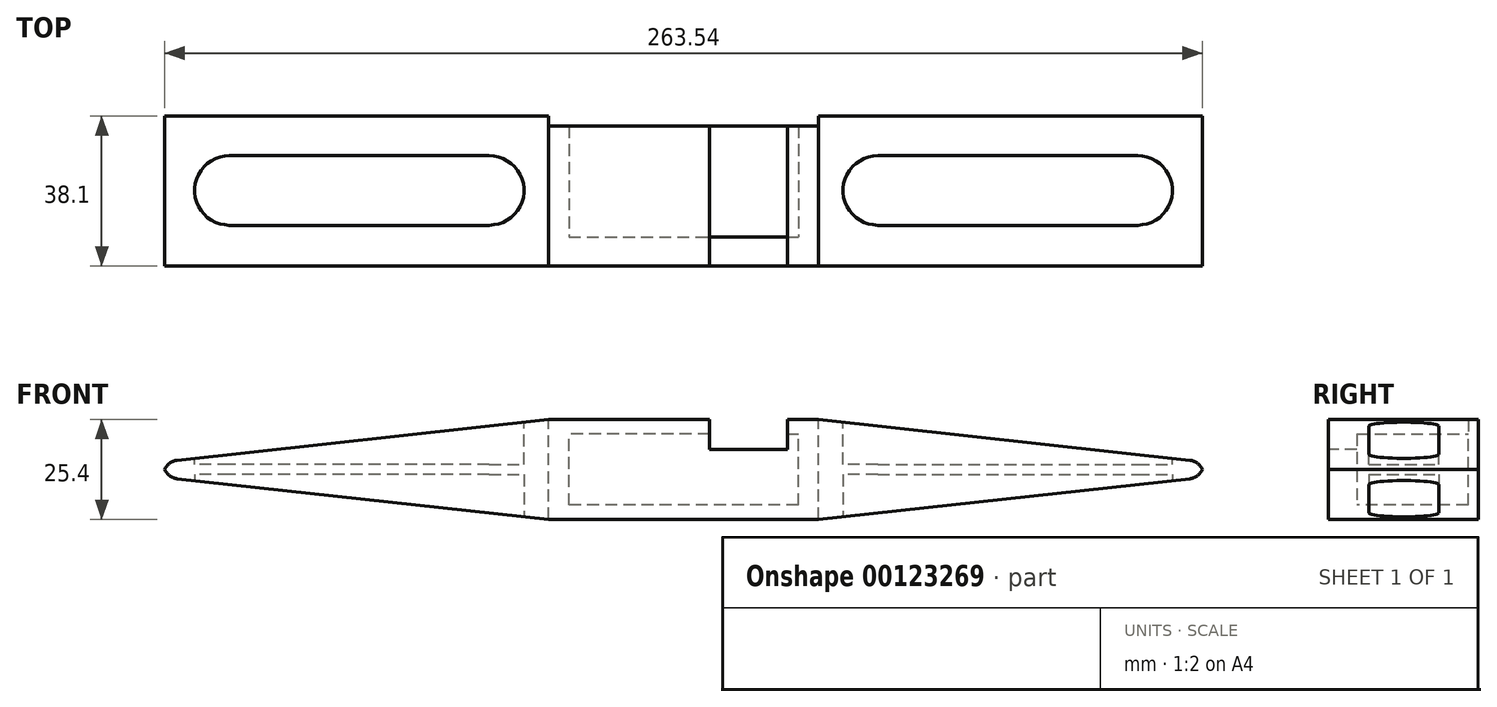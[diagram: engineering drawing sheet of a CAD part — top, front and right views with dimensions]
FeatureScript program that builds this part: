
annotation { "Feature Type Name" : "Feature", "Feature Type Description" : "" }
export const myFeature = defineFeature(function(context is Context, id is Id, definition is map)
    precondition{}
    {
        {
            var Q0;
            Q0=qCreatedBy(makeId("Front.planeOp"),FACE);
            var sketch = newSketch(context, id + "F0", { "sketchPlane" : qUnion([Q0])});
            skLineSegment(sketch, "E0", {"start": v(-77.8, 2.35) * mm, "end": v(16.5, 12.7) * mm});
            skLineSegment(sketch, "E1", {"start": v(16.5, 12.7) * mm, "end": v(50.8, 12.7) * mm});
            skLineSegment(sketch, "E2", {"start": v(50.8, 12.7) * mm, "end": v(50.8, 0) * mm});
            skArc(sketch, "E3", {"start": v(-77.8, 2.35) * mm, "mid": v(-79.7, 1.6) * mm, "end": v(-80.97, 0) * mm});
            skLineSegment(sketch, "E4", {"start": v(-80.97, 0) * mm, "end": v(50.8, 0) * mm});
            skSolve(sketch);
        }
        {
            var Q0;
            Q0 = qSketchRegion(id + "F0", true);
            extrude(context, id + "F1", {"entities" : qUnion([Q0]), "endBound" : BoundingType.SYMMETRIC, "depth" : 38.1 * mm});
        }
        {
            var Q0;
            Q0=qCreatedBy(makeId("Top.planeOp"),FACE);
            cPlane(context, id + "F2", {"entities" : qUnion([Q0]), "cplaneType" : CPlaneType.OFFSET, "offset" : 12.7 * mm, "width" : 152.4 * mm, "height" : 152.4 * mm});
        }
        {
            var Q0;
            Q0=qCreatedBy(id+"F2.planeOp",FACE);
            var sketch = newSketch(context, id + "F3", { "sketchPlane" : qUnion([Q0])});
            skLineSegment(sketch, "E5", {"start": v(1.44, -8.7) * mm, "end": v(-64.6, -8.7) * mm});
            skLineSegment(sketch, "E6", {"start": v(1.44, 9.02) * mm, "end": v(-64.6, 9.02) * mm});
            skArc(sketch, "E7", {"start": v(1.44, -8.7) * mm, "mid": v(10.3, 0.16) * mm, "end": v(1.44, 9.02) * mm});
            skArc(sketch, "E8", {"start": v(-64.6, -8.7) * mm, "mid": v(-73.46, 0.16) * mm, "end": v(-64.6, 9.02) * mm});
            skSolve(sketch);
        }
        {
            var Q0;
            Q0 = qSketchRegion(id + "F3", true);
            extrude(context, id + "F4", {"entities" : qUnion([Q0]), "operationType" : NewBodyOperationType.REMOVE, "oppositeDirection" : true, "depth" : 11.43 * mm});
        }
        {
            var Q0;
            Q0=makeQuery(id+"F1.opExtrude","SWEPT_BODY",BODY,{"disambiguationData":[OSD([sQuery(id+"F0.wireOp",EDGE,"E0"),sQuery(id+"F0.wireOp",EDGE,"E1"),sQuery(id+"F0.wireOp",EDGE,"E2"),sQuery(id+"F0.wireOp",EDGE,"E3"),sQuery(id+"F0.wireOp",EDGE,"E4")])]});
            var Q1;
            Q1=qCreatedBy(makeId("Top.planeOp"),FACE);
            mirror(context, id + "F5", {"operationType" : NewBodyOperationType.ADD, "entities" : qUnion([Q0]), "mirrorPlane" : qUnion([Q1])});
        }
        {
            var Q0;
            Q0=qCreatedBy(makeId("Right.planeOp"),FACE);
            cPlane(context, id + "F6", {"entities" : qUnion([Q0]), "cplaneType" : CPlaneType.OFFSET, "offset" : 50.8 * mm, "width" : 152.4 * mm, "height" : 152.4 * mm});
        }
        {
            var Q0;
            Q0=makeQuery(id+"F1.opExtrude","SWEPT_BODY",BODY,{"disambiguationData":[OSD([sQuery(id+"F0.wireOp",EDGE,"E0"),sQuery(id+"F0.wireOp",EDGE,"E1"),sQuery(id+"F0.wireOp",EDGE,"E2"),sQuery(id+"F0.wireOp",EDGE,"E3"),sQuery(id+"F0.wireOp",EDGE,"E4")])]});
            var Q1;
            Q1=qCreatedBy(id+"F6.planeOp",FACE);
            mirror(context, id + "F7", {"operationType" : NewBodyOperationType.ADD, "entities" : qUnion([Q0]), "mirrorPlane" : qUnion([Q1])});
        }
        {
            var Q0;
            Q0=qCreatedBy(makeId("Front.planeOp"),FACE);
            var sketch = newSketch(context, id + "F8", { "sketchPlane" : qUnion([Q0])});
            skLineSegment(sketch, "E9.bottom", {"start": v(21.65, 9.04) * mm, "end": v(79.95, 9.04) * mm});
            skLineSegment(sketch, "E9.top", {"start": v(21.65, -9.04) * mm, "end": v(79.95, -9.04) * mm});
            skLineSegment(sketch, "E9.left", {"start": v(21.65, 9.04) * mm, "end": v(21.65, -9.04) * mm});
            skLineSegment(sketch, "E9.right", {"start": v(79.95, 9.04) * mm, "end": v(79.95, -9.04) * mm});
            skPoint(sketch, "E9.middle", {"position": v(50.8, 0) * mm});
            skSolve(sketch);
        }
        {
            var Q0;
            Q0 = qSketchRegion(id + "F8", true);
            extrude(context, id + "F9", {"entities" : qUnion([Q0]), "operationType" : NewBodyOperationType.REMOVE, "endBound" : BoundingType.THROUGH_ALL, "oppositeDirection" : true, "depth" : 25.4 * mm, "hasSecondDirection" : true, "secondDirectionOppositeDirection" : false, "secondDirectionDepth" : 11.74 * mm});
        }
        {
            var Q0;
            Q0=qCreatedBy(makeId("Front.planeOp"),FACE);
            cPlane(context, id + "F10", {"entities" : qUnion([Q0]), "cplaneType" : CPlaneType.OFFSET, "offset" : 19.05 * mm, "oppositeDirection" : true, "width" : 152.4 * mm, "height" : 152.4 * mm});
        }
        {
            var Q0;
            Q0=qCreatedBy(id+"F10.planeOp",FACE);
            var sketch = newSketch(context, id + "F11", { "sketchPlane" : qUnion([Q0])});
            skLineSegment(sketch, "E10", {"start": v(16.5, -12.7) * mm, "end": v(16.5, 12.7) * mm});
            skLineSegment(sketch, "E11", {"start": v(85.1, -12.7) * mm, "end": v(85.1, 12.7) * mm});
            skLineSegment(sketch, "E12", {"start": v(85.1, -12.7) * mm, "end": v(16.5, -12.7) * mm});
            skLineSegment(sketch, "E13", {"start": v(85.1, 12.7) * mm, "end": v(16.5, 12.7) * mm});
            skSolve(sketch);
        }
        {
            var Q0;
            Q0 = qSketchRegion(id + "F11", true);
            extrude(context, id + "F12", {"entities" : qUnion([Q0]), "operationType" : NewBodyOperationType.REMOVE, "depth" : 2.54 * mm});
        }
        {
            var Q0;
            Q0=qCreatedBy(id+"F2.planeOp",FACE);
            var sketch = newSketch(context, id + "F13", { "sketchPlane" : qUnion([Q0])});
            skLineSegment(sketch, "E14.bottom", {"start": v(57.42, 18.97) * mm, "end": v(77.24, 18.97) * mm});
            skLineSegment(sketch, "E14.top", {"start": v(57.42, -25.93) * mm, "end": v(77.24, -25.93) * mm});
            skLineSegment(sketch, "E14.left", {"start": v(57.42, 18.97) * mm, "end": v(57.42, -25.93) * mm});
            skLineSegment(sketch, "E14.right", {"start": v(77.24, 18.97) * mm, "end": v(77.24, -25.93) * mm});
            skSolve(sketch);
        }
        {
            var Q0;
            Q0 = qSketchRegion(id + "F13", true);
            extrude(context, id + "F14", {"entities" : qUnion([Q0]), "operationType" : NewBodyOperationType.REMOVE, "oppositeDirection" : true, "depth" : 7.62 * mm});
        }
    });
